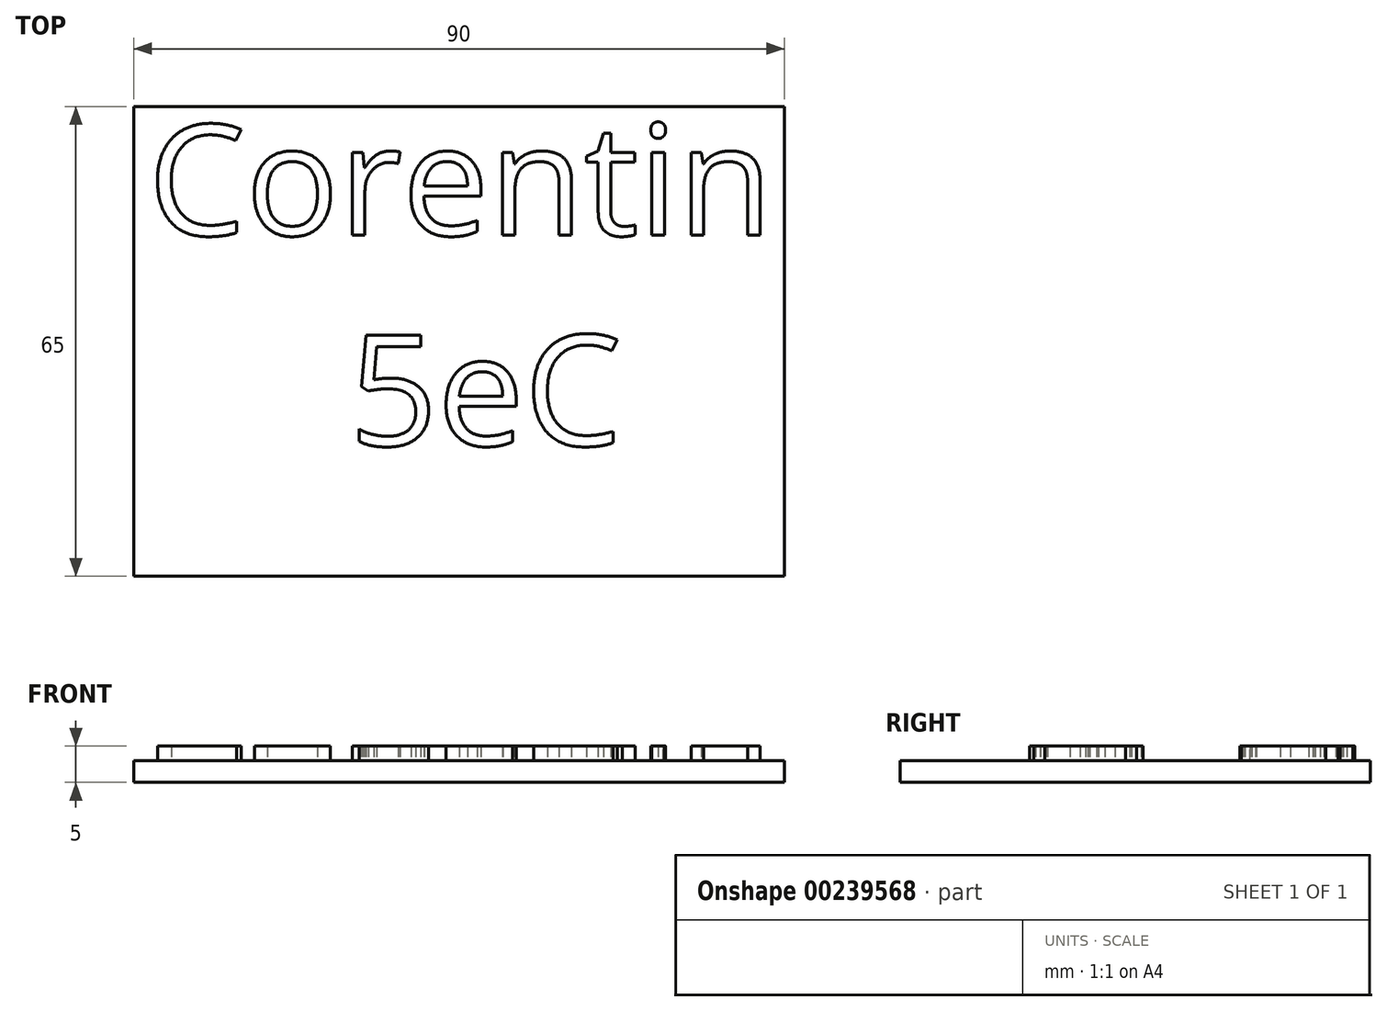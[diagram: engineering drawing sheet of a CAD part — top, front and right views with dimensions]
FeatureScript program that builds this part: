
annotation { "Feature Type Name" : "Feature", "Feature Type Description" : "" }
export const myFeature = defineFeature(function(context is Context, id is Id, definition is map)
    precondition{}
    {
        {
            var Q0;
            Q0=qCreatedBy(makeId("Top.planeOp"),FACE);
            var sketch = newSketch(context, id + "F0", { "sketchPlane" : qUnion([Q0])});
            skLineSegment(sketch, "E0.bottom", {"start": v(0, 0) * mm, "end": v(90, 0) * mm});
            skLineSegment(sketch, "E0.top", {"start": v(0, -65) * mm, "end": v(90, -65) * mm});
            skLineSegment(sketch, "E0.left", {"start": v(0, 0) * mm, "end": v(0, -65) * mm});
            skLineSegment(sketch, "E0.right", {"start": v(90, 0) * mm, "end": v(90, -65) * mm});
            skSolve(sketch);
        }
        {
            var Q0;
            Q0=makeQuery(id+"F0.imprint","IMPRINT",FACE,{"disambiguationData":[TD([[makeQuery(id+"F0.imprint","IMPRINT",EDGE,{"derivedFrom":sQuery(id+"F0.wireOp",EDGE,"E0.bottom")}),-1.0]])]});
            extrude(context, id + "F1", {"entities" : qUnion([Q0]), "depth" : 3 * mm});
        }
        {
            var Q0;
            Q0=makeQuery(id+"F1.opExtrude","CAP_FACE",FACE,{"disambiguationData":[OSD([sQuery(id+"F0.wireOp",EDGE,"E0.bottom"),sQuery(id+"F0.wireOp",EDGE,"E0.top"),sQuery(id+"F0.wireOp",EDGE,"E0.left"),sQuery(id+"F0.wireOp",EDGE,"E0.right")])],"isStart":false});
            var sketch = newSketch(context, id + "F2", { "sketchPlane" : qUnion([Q0])});
            skText(sketch, "E1", { "text": "Corentin\n     5eC", "fontName": "OpenSans-Regular.ttf"});
            const initialGuessF2  = {"E1": [0.002, -0.01782, 1, 0, 0.0154]};
            skSetInitialGuess(sketch, initialGuessF2);
            skSolve(sketch);
        }
        {
            var Q0;
            Q0 = qSketchRegion(id + "F2", true);
            extrude(context, id + "F3", {"entities" : qUnion([Q0]), "operationType" : NewBodyOperationType.ADD, "depth" : 2 * mm});
        }
    });
